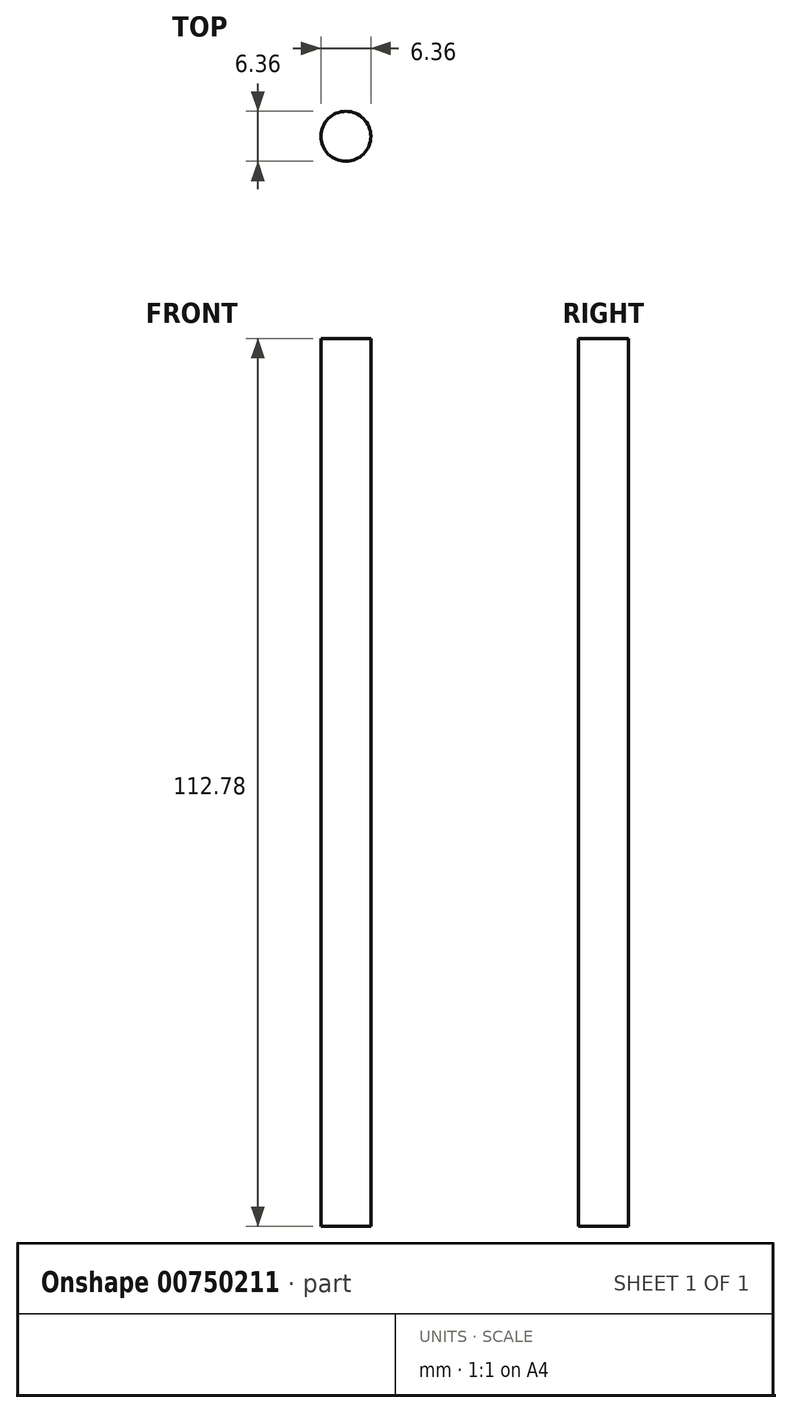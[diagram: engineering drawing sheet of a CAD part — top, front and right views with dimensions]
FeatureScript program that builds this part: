
annotation { "Feature Type Name" : "Feature", "Feature Type Description" : "" }
export const myFeature = defineFeature(function(context is Context, id is Id, definition is map)
    precondition{}
    {
        {
            var Q0;
            Q0=qCreatedBy(makeId("Top.planeOp"),FACE);
            var sketch = newSketch(context, id + "F0", { "sketchPlane" : qUnion([Q0])});
            skCircle(sketch, "E0", {"center": v(0, 0) * mm, "radius": 3.18 * mm});
            skSolve(sketch);
        }
        {
            var Q0;
            Q0=makeQuery(id+"F0.imprint","IMPRINT",FACE,{"disambiguationData":[TD([[makeQuery(id+"F0.imprint","IMPRINT",EDGE,{"derivedFrom":sQuery(id+"F0.wireOp",EDGE,"E0")}),1.0]])]});
            extrude(context, id + "F1", {"entities" : qUnion([Q0]), "depth" : 112.78 * mm, "offsetDistance" : 25.4 * mm});
        }
    });
